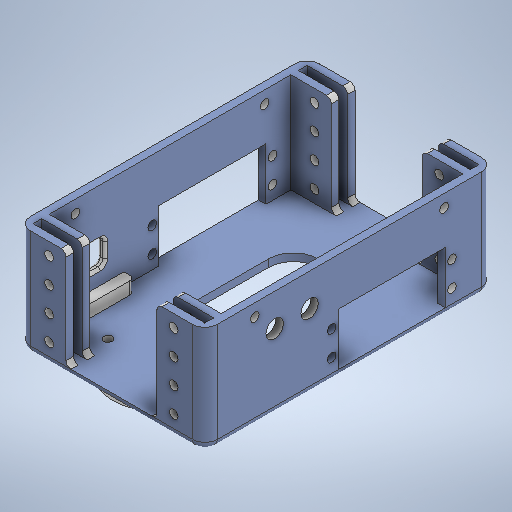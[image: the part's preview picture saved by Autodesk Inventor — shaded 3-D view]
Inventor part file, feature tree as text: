
AUTODESK INVENTOR PART (.ipt)
format: ipt  version: 2025 (Build 290162000, 162)  size: 1,124,352 bytes
history: native  units: mm
features: extrude x10, sketch x10, fillet x8
ambient origin geometry x8: Origin, YZ Plane, XZ Plane, XY Plane, X Axis, Y Axis, Z Axis, Center Point
bodies: Solide1 (feature_tree)
feature tree (28):
  extrude  "Extrusion1"  Depth=3.0mm TaperAngle=0.0deg
  extrude  "Extrusion2"  Depth=3.0mm
  extrude  "Extrusion3"  Depth=40.0mm TaperAngle=0.0deg
  fillet  "Congé1"  Radius=3.0mm
  fillet  "Congé2"  Radius=3.0mm
  extrude  "Extrusion5"  Depth=100.0mm TaperAngle=0.0deg
  fillet  "Congé5"  Radius=43.0mm
  extrude  "Extrusion6"  Depth=21.0mm
  fillet  "Congé6"  Radius=75.0mm
  fillet  "Congé7"  Radius=116.0mm
  extrude  "Extrusion7"  Depth=5.0mm
  extrude  "Extrusion8"  Depth=3.0mm
  extrude  "Extrusion9"  Depth=3.5mm
  fillet  "Congé8"  Radius=60.0mm
  fillet  "Congé9"  Radius=30.0mm
  extrude  "Extrusion10"  Depth=3.0mm TaperAngle=0.0deg
  extrude  "Extrusion11"  Depth=10.0mm
  fillet  "Congé10"  Radius=18.25mm
  sketch  "Esquisse1"
  sketch  "Esquisse2"
  sketch  "Esquisse3"
  sketch  "Esquisse5"
  sketch  "Esquisse6"
  sketch  "Esquisse7"
  sketch  "Esquisse8"
  sketch  "Esquisse9"
  sketch  "Esquisse10"
  sketch  "Esquisse11"
